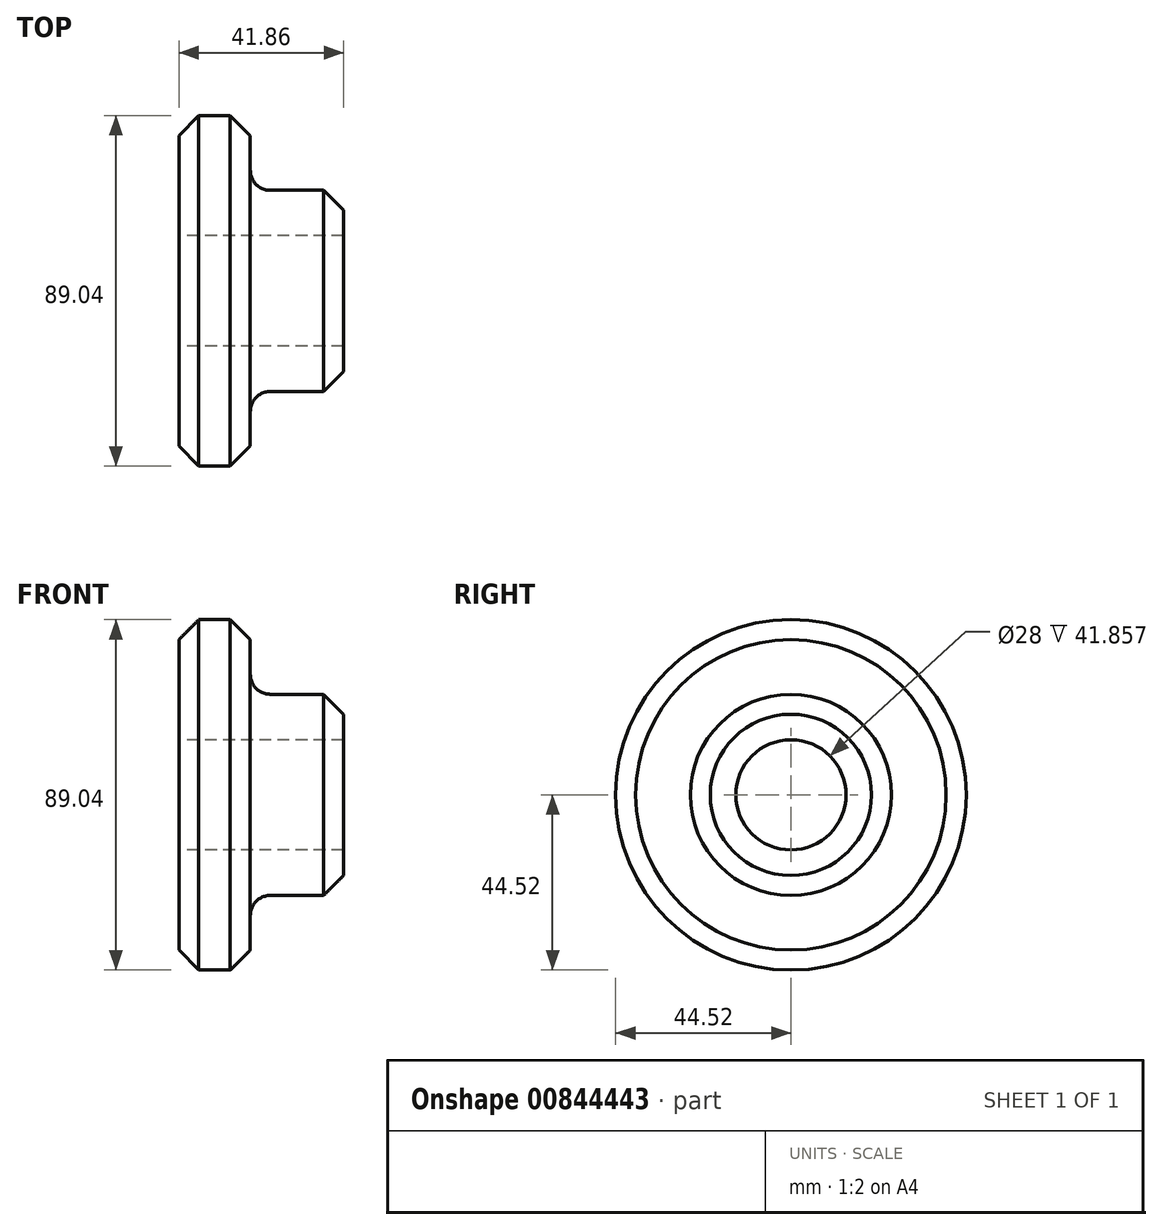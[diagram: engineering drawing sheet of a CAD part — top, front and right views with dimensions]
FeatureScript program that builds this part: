
annotation { "Feature Type Name" : "Feature", "Feature Type Description" : "" }
export const myFeature = defineFeature(function(context is Context, id is Id, definition is map)
    precondition{}
    {
        {
            var Q0;
            Q0=qCreatedBy(makeId("Front.planeOp"),FACE);
            var sketch = newSketch(context, id + "F0", { "sketchPlane" : qUnion([Q0])});
            skLineSegment(sketch, "E0", {"start": v(0, 44.52) * mm, "end": v(18.15, 44.52) * mm});
            skLineSegment(sketch, "E1", {"start": v(18.15, 44.52) * mm, "end": v(18.15, 25.56) * mm});
            skLineSegment(sketch, "E2", {"start": v(18.15, 25.56) * mm, "end": v(41.86, 25.56) * mm});
            skLineSegment(sketch, "E3", {"start": v(41.86, 25.56) * mm, "end": v(41.86, 14) * mm});
            skLineSegment(sketch, "E4", {"start": v(41.86, 14) * mm, "end": v(0, 14) * mm});
            skLineSegment(sketch, "E5", {"start": v(0, 14) * mm, "end": v(0, 44.52) * mm});
            skLineSegment(sketch, "E6", {"start": v(0, 0) * mm, "end": v(43.34, 0) * mm, "construction": true});
            skSolve(sketch);
        }
        {
            var Q0;
            Q0=makeQuery(id+"F0.imprint","IMPRINT",FACE,{"disambiguationData":[TD([[makeQuery(id+"F0.imprint","IMPRINT",EDGE,{"derivedFrom":sQuery(id+"F0.wireOp",EDGE,"E0")}),-1.0]])]});
            var Q1;
            Q1=sQuery(id+"F0.wireOp",EDGE,"E6");
            revolve(context, id + "F1", {"surfaceOperationType" : NewSurfaceOperationType.NEW, "entities" : qUnion([Q0]), "axis" : qUnion([Q1]), "revolveType" : RevolveType.FULL});
        }
        {
            var Q0;
            Q0=makeQuery(id+"F1.opRevolve","SWEPT_EDGE",EDGE,{"disambiguationData":[OSD([sQuery(id+"F0.wireOp",EDGE,"E1"),sQuery(id+"F0.wireOp",EDGE,"E2")])]});
            fillet(context, id + "F2", {"entities" : qUnion([Q0]), "radius" : 5.08 * mm, "tangentPropagation" : true, "allowEdgeOverflow" : false});
        }
        {
            var Q0;
            Q0=makeQuery(id+"F1.opRevolve","SWEPT_EDGE",EDGE,{"disambiguationData":[OSD([sQuery(id+"F0.wireOp",EDGE,"E2"),sQuery(id+"F0.wireOp",EDGE,"E3")])]});
            var Q1;
            Q1=makeQuery(id+"F1.opRevolve","SWEPT_EDGE",EDGE,{"disambiguationData":[OSD([sQuery(id+"F0.wireOp",EDGE,"E0"),sQuery(id+"F0.wireOp",EDGE,"E1")])]});
            var Q2;
            Q2=makeQuery(id+"F1.opRevolve","SWEPT_EDGE",EDGE,{"disambiguationData":[OSD([sQuery(id+"F0.wireOp",EDGE,"E0"),sQuery(id+"F0.wireOp",EDGE,"E5")])]});
            chamfer(context, id + "F3", {"entities" : qUnion([Q0, Q1, Q2]), "width" : 5.08 * mm, "tangentPropagation" : true});
        }
        {
            var Q0;
            Q0=qCreatedBy(makeId("Front.planeOp"),FACE);
            var sketch = newSketch(context, id + "F4", { "sketchPlane" : qUnion([Q0])});
            skLineSegment(sketch, "E7.bottom", {"start": v(38.12, 82.91) * mm, "end": v(-29.3, 82.91) * mm});
            skLineSegment(sketch, "E7.top", {"start": v(38.12, 49.11) * mm, "end": v(-29.3, 49.11) * mm});
            skLineSegment(sketch, "E7.left", {"start": v(38.12, 82.91) * mm, "end": v(38.12, 49.11) * mm});
            skLineSegment(sketch, "E7.right", {"start": v(-29.3, 82.91) * mm, "end": v(-29.3, 49.11) * mm});
            skSolve(sketch);
        }
        {
            var Q0;
            Q0=sQuery(id+"F4.wireOp",EDGE,"E7.left");
            extrude(context, id + "F5", {"bodyType" : ToolBodyType.SURFACE, "surfaceEntities" : qUnion([Q0]), "depth" : 25.4 * mm, "offsetDistance" : 25.4 * mm});
        }
    });
